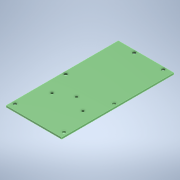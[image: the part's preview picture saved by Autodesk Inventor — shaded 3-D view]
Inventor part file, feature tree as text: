
AUTODESK INVENTOR PART (.ipt)
format: ipt  version: 2021 (Build 250183000, 183)  size: 126,464 bytes
history: native  units: mm
features: sketch x2, hole x2, extrude x1
ambient origin geometry x8: Origin, YZ Plane, XZ Plane, XY Plane, X Axis, Y Axis, Z Axis, Center Point
bodies: Solid1 (feature_tree)
feature tree (5):
  sketch  "Sketch1"  dims[d0=53.34mm d1=107.95mm]
  extrude  "Extrusion1"  Depth=107.95mm
  hole  "Hole1"  [1 undecoded]
  hole  "Hole2"  [1 undecoded]
  sketch  "Sketch2"  dims[d2=3.0mm d3=5.5mm d4=5.5mm d5=3.34mm d6=53.34mm d7=54.61mm d8=2.54mm d9=2.54mm d10=7.62mm d11=17.78mm d12=1.65mm d13=0.0mm d14=3.2mm d15=6.0mm d16=4.0mm d17=2.0mm d18=90.0deg d19=8.0mm d20=20.594885mm d21=23.67mm d22=26.67mm d23=34.4mm d24=150.0deg d25=30.0deg d26=2.58mm d27=6.0mm d28=4.0mm d29=2.0mm d30=90.0deg d31=8.0mm d32=20.594885mm]
note: 2 required parameter values undecoded (feature->parameter linkage not recoverable at this tier; creation-order binding heuristic only, values carry confidence <= 0.55)
